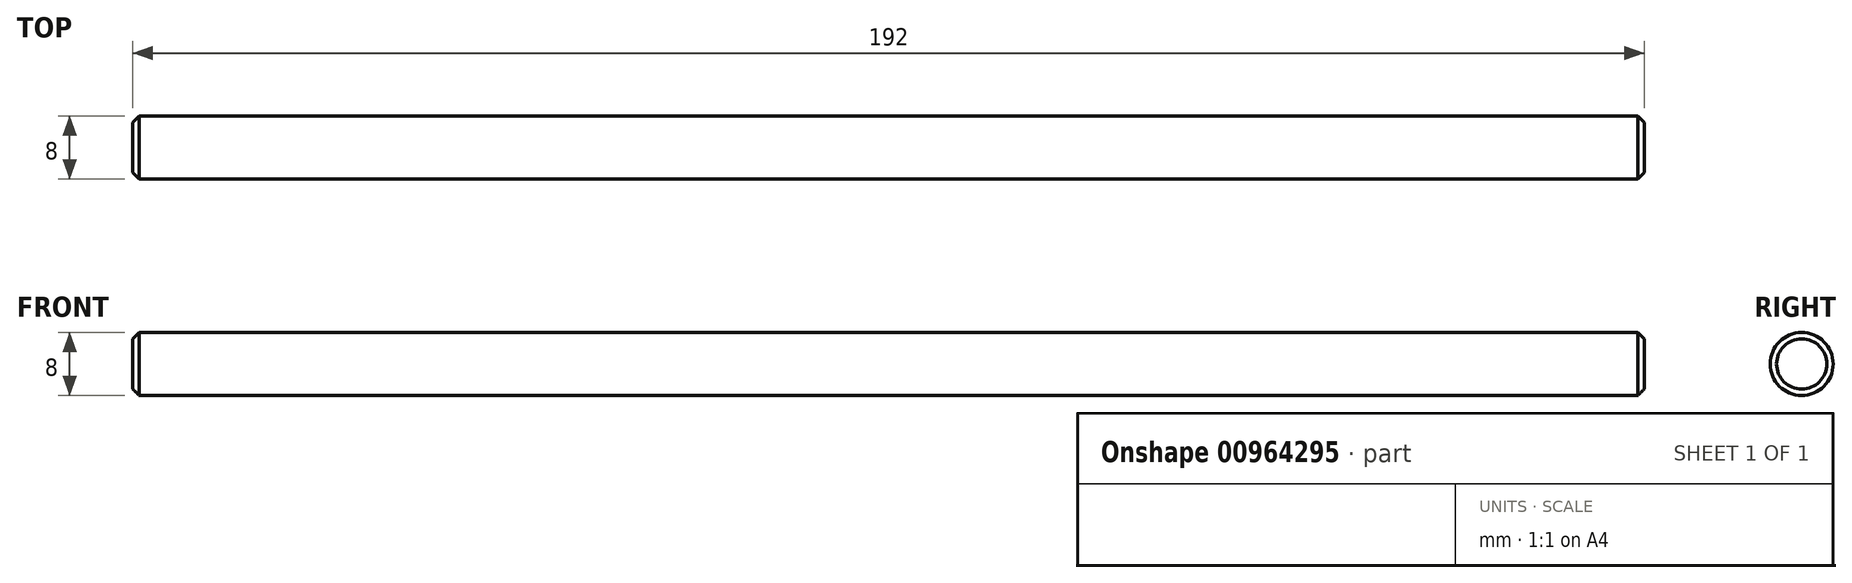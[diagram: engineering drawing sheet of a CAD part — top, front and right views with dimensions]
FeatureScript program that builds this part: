
annotation { "Feature Type Name" : "Feature", "Feature Type Description" : "" }
export const myFeature = defineFeature(function(context is Context, id is Id, definition is map)
    precondition{}
    {
        {
            var Q0;
            Q0=qCreatedBy(makeId("Right.planeOp"),FACE);
            var sketch = newSketch(context, id + "F0", { "sketchPlane" : qUnion([Q0])});
            skCircle(sketch, "E0", {"center": v(0, 0) * mm, "radius": 4 * mm});
            skSolve(sketch);
        }
        {
            var Q0;
            Q0 = qSketchRegion(id + "F0", true);
            extrude(context, id + "F1", {"entities" : qUnion([Q0]), "depth" : 192 * mm, "offsetDistance" : 25 * mm, "symmetric" : true});
        }
        {
            var Q0;
            Q0=makeQuery(id+"F1.opExtrude","CAP_EDGE",EDGE,{"disambiguationData":[OSD([sQuery(id+"F0.wireOp",EDGE,"E0")])],"isStart":false});
            var Q1;
            Q1=makeQuery(id+"F1.opExtrude","CAP_EDGE",EDGE,{"disambiguationData":[OSD([sQuery(id+"F0.wireOp",EDGE,"E0")])],"isStart":true});
            chamfer(context, id + "F2", {"entities" : qUnion([Q0, Q1]), "width" : .81 * mm, "tangentPropagation" : true});
        }
    });
